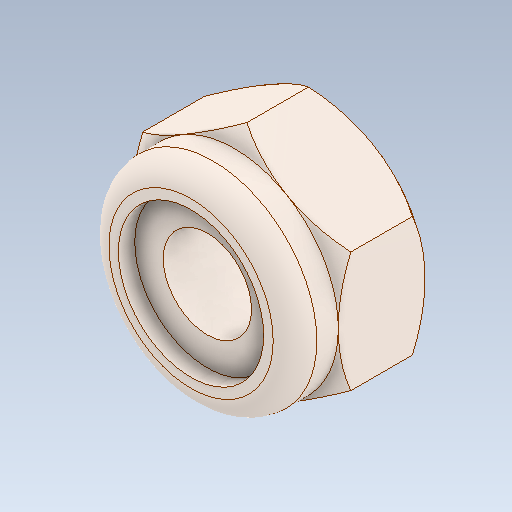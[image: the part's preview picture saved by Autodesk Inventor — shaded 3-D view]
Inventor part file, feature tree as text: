
AUTODESK INVENTOR PART (.ipt)
format: ipt  version: 2020.2 (Build 242310000, 310)  size: 169,984 bytes
history: native  units: in
note: dims shown in document units (in); Inventor stores cm internally (conversion verified against a paired STEP export)
features: fillet x1
ambient origin geometry x8: Origin, YZ Plane, XZ Plane, XY Plane, X Axis, Y Axis, Z Axis, Center Point
bodies: Solid1 (feature_tree)
feature tree (1):
  fillet  "Fillet1"  [1 undecoded]
note: 1 required parameter value undecoded (feature->parameter linkage not recoverable at this tier; creation-order binding heuristic only, values carry confidence <= 0.55)
